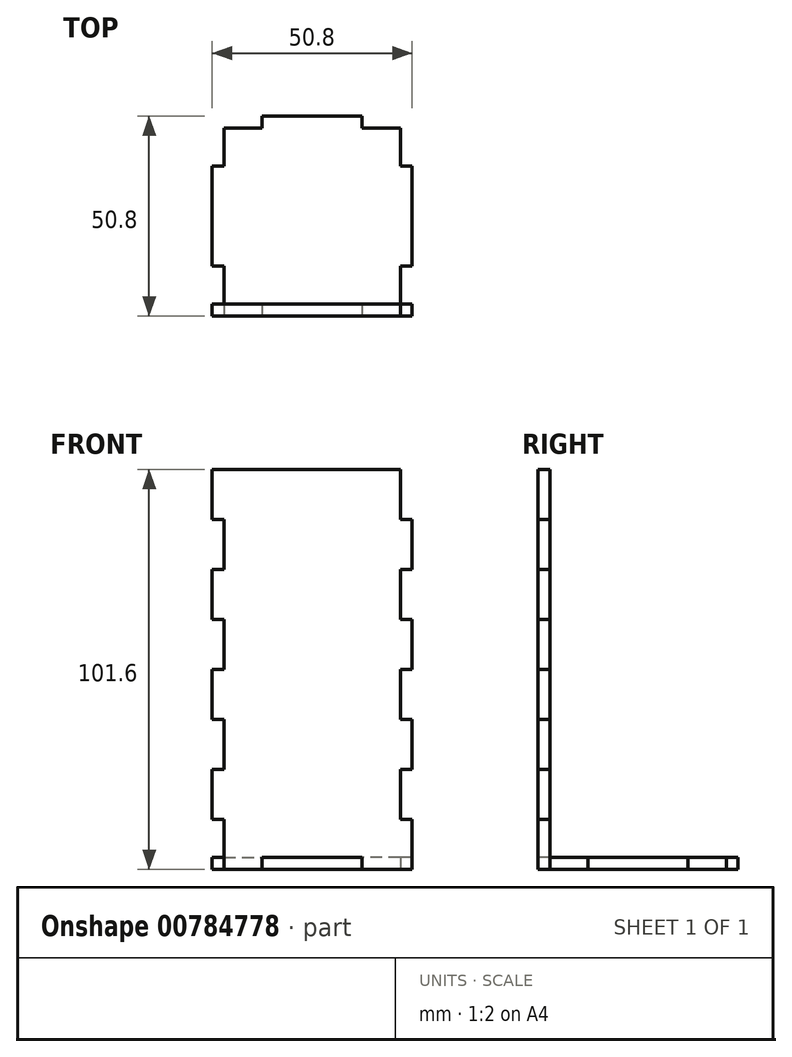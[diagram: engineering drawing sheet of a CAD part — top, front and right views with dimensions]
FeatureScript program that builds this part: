
annotation { "Feature Type Name" : "Feature", "Feature Type Description" : "" }
export const myFeature = defineFeature(function(context is Context, id is Id, definition is map)
    precondition{}
    {
        {
            assignVariable(context, id + "F0", {"variableType" : VariableType.LENGTH, "name" : "thk", "lengthValue" : 3 * mm});
        }
        {
            var Q0;
            Q0=qCreatedBy(makeId("Top.planeOp"),FACE);
            var sketch = newSketch(context, id + "F1", { "sketchPlane" : qUnion([Q0])});
            skLineSegment(sketch, "E0.bottom", {"start": v(25.4, 25.4) * mm, "end": v(-25.4, 25.4) * mm});
            skLineSegment(sketch, "E0.top", {"start": v(25.4, -25.4) * mm, "end": v(-25.4, -25.4) * mm});
            skLineSegment(sketch, "E0.left", {"start": v(25.4, 25.4) * mm, "end": v(25.4, -25.4) * mm});
            skLineSegment(sketch, "E0.right", {"start": v(-25.4, 25.4) * mm, "end": v(-25.4, -25.4) * mm});
            skPoint(sketch, "E0.middle", {"position": v(0, 0) * mm});
            skLineSegment(sketch, "E1", {"start": v(0, 0) * mm, "end": v(-25.4, 0) * mm, "construction": true});
            skLineSegment(sketch, "E2.bottom", {"start": v(-25.4, 25.4) * mm, "end": v(-22.4, 25.4) * mm});
            skLineSegment(sketch, "E2.top", {"start": v(-25.4, 12.7) * mm, "end": v(-22.4, 12.7) * mm});
            skLineSegment(sketch, "E2.left", {"start": v(-25.4, 25.4) * mm, "end": v(-25.4, 12.7) * mm});
            skLineSegment(sketch, "E2.right", {"start": v(-22.4, 25.4) * mm, "end": v(-22.4, 12.7) * mm});
            skLineSegment(sketch, "E3.bottom", {"start": v(-25.4, 25.4) * mm, "end": v(-12.7, 25.4) * mm});
            skLineSegment(sketch, "E3.top", {"start": v(-25.4, 22.4) * mm, "end": v(-12.7, 22.4) * mm});
            skLineSegment(sketch, "E3.left", {"start": v(-25.4, 25.4) * mm, "end": v(-25.4, 22.4) * mm});
            skLineSegment(sketch, "E3.right", {"start": v(-12.7, 25.4) * mm, "end": v(-12.7, 22.4) * mm});
            skLineSegment(sketch, "E4.1.0", {"start": v(-25.4, -25.4) * mm, "end": v(-25.4, -22.4) * mm});
            skLineSegment(sketch, "E4.1.1", {"start": v(-25.4, -22.4) * mm, "end": v(-12.7, -22.4) * mm});
            skLineSegment(sketch, "E4.1.2", {"start": v(-25.4, -25.4) * mm, "end": v(-22.4, -25.4) * mm});
            skLineSegment(sketch, "E4.1.3", {"start": v(-22.4, -25.4) * mm, "end": v(-22.4, -12.7) * mm});
            skLineSegment(sketch, "E4.1.4", {"start": v(-25.4, -25.4) * mm, "end": v(-25.4, -12.7) * mm});
            skLineSegment(sketch, "E4.1.5", {"start": v(-25.4, -12.7) * mm, "end": v(-22.4, -12.7) * mm});
            skLineSegment(sketch, "E4.1.6", {"start": v(-12.7, -25.4) * mm, "end": v(-12.7, -22.4) * mm});
            skLineSegment(sketch, "E4.1.7", {"start": v(-25.4, -25.4) * mm, "end": v(-12.7, -25.4) * mm});
            skLineSegment(sketch, "E4.2.0", {"start": v(25.4, -25.4) * mm, "end": v(22.4, -25.4) * mm});
            skLineSegment(sketch, "E4.2.1", {"start": v(22.4, -25.4) * mm, "end": v(22.4, -12.7) * mm});
            skLineSegment(sketch, "E4.2.2", {"start": v(25.4, -25.4) * mm, "end": v(25.4, -22.4) * mm});
            skLineSegment(sketch, "E4.2.3", {"start": v(25.4, -22.4) * mm, "end": v(12.7, -22.4) * mm});
            skLineSegment(sketch, "E4.2.4", {"start": v(25.4, -25.4) * mm, "end": v(12.7, -25.4) * mm});
            skLineSegment(sketch, "E4.2.5", {"start": v(12.7, -25.4) * mm, "end": v(12.7, -22.4) * mm});
            skLineSegment(sketch, "E4.2.6", {"start": v(25.4, -12.7) * mm, "end": v(22.4, -12.7) * mm});
            skLineSegment(sketch, "E4.2.7", {"start": v(25.4, -25.4) * mm, "end": v(25.4, -12.7) * mm});
            skLineSegment(sketch, "E4.3.0", {"start": v(25.4, 25.4) * mm, "end": v(25.4, 22.4) * mm});
            skLineSegment(sketch, "E4.3.1", {"start": v(25.4, 22.4) * mm, "end": v(12.7, 22.4) * mm});
            skLineSegment(sketch, "E4.3.2", {"start": v(25.4, 25.4) * mm, "end": v(22.4, 25.4) * mm});
            skLineSegment(sketch, "E4.3.3", {"start": v(22.4, 25.4) * mm, "end": v(22.4, 12.7) * mm});
            skLineSegment(sketch, "E4.3.4", {"start": v(25.4, 25.4) * mm, "end": v(25.4, 12.7) * mm});
            skLineSegment(sketch, "E4.3.5", {"start": v(25.4, 12.7) * mm, "end": v(22.4, 12.7) * mm});
            skLineSegment(sketch, "E4.3.6", {"start": v(12.7, 25.4) * mm, "end": v(12.7, 22.4) * mm});
            skLineSegment(sketch, "E4.3.7", {"start": v(25.4, 25.4) * mm, "end": v(12.7, 25.4) * mm});
            skSolve(sketch);
        }
        {
            var Q0;
            {var subQ13=sQuery(id+"F1.wireOp",EDGE,"E2.top");Q0=makeQuery(id+"F1.imprint","IMPRINT",FACE,{"disambiguationData":[TD([[makeQuery(id+"F1.imprint","IMPRINT",EDGE,{"derivedFrom":subQ13}),-1.0]])]});}
            extrude(context, id + "F2", {"entities" : qUnion([Q0]), "depth" : getVariable(context, 'thk'), "offsetDistance" : 25.4 * mm});
        }
        {
            var Q0;
            Q0=makeQuery(id+"F2.opExtrude","SWEPT_FACE",FACE,{"disambiguationData":[OSD([sQuery(id+"F1.wireOp",EDGE,"E0.top")])]});
            var sketch = newSketch(context, id + "F3", { "sketchPlane" : qUnion([Q0])});
            skLineSegment(sketch, "E5.bottom", {"start": v(-25.4, 0) * mm, "end": v(25.4, 0) * mm});
            skLineSegment(sketch, "E5.top", {"start": v(-25.4, 101.6) * mm, "end": v(25.4, 101.6) * mm});
            skLineSegment(sketch, "E5.left", {"start": v(-25.4, 0) * mm, "end": v(-25.4, 101.6) * mm});
            skLineSegment(sketch, "E5.right", {"start": v(25.4, 0) * mm, "end": v(25.4, 101.6) * mm});
            skLineSegment(sketch, "E6", {"start": v(0, 101.6) * mm, "end": v(0, 0) * mm, "construction": true});
            skLineSegment(sketch, "E7", {"start": v(22.4, 101.6) * mm, "end": v(22.4, 0) * mm});
            skLineSegment(sketch, "E8", {"start": v(22.4, 88.9) * mm, "end": v(25.4, 88.9) * mm});
            skLineSegment(sketch, "E9.1.0.0", {"start": v(22.4, 76.2) * mm, "end": v(25.4, 76.2) * mm});
            skLineSegment(sketch, "E9.2.0.0", {"start": v(22.4, 63.5) * mm, "end": v(25.4, 63.5) * mm});
            skLineSegment(sketch, "E9.direction1", {"start": v(22.4, 88.9) * mm, "end": v(22.4, 76.2) * mm, "construction": true});
            skLineSegment(sketch, "E10.0.3.0", {"start": v(22.4, 50.8) * mm, "end": v(25.4, 50.8) * mm});
            skLineSegment(sketch, "E10.0.4.0", {"start": v(22.4, 38.1) * mm, "end": v(25.4, 38.1) * mm});
            skLineSegment(sketch, "E10.0.5.0", {"start": v(22.4, 25.4) * mm, "end": v(25.4, 25.4) * mm});
            skLineSegment(sketch, "E10.0.6.0", {"start": v(22.4, 12.7) * mm, "end": v(25.4, 12.7) * mm});
            skLineSegment(sketch, "E11.MirrorCS", {"start": v(-22.4, 50.8) * mm, "end": v(-25.4, 50.8) * mm});
            skLineSegment(sketch, "E12.MirrorCS", {"start": v(-22.4, 12.7) * mm, "end": v(-25.4, 12.7) * mm});
            skLineSegment(sketch, "E13.MirrorCS", {"start": v(-22.4, 63.5) * mm, "end": v(-25.4, 63.5) * mm});
            skLineSegment(sketch, "E14.MirrorCS", {"start": v(-22.4, 38.1) * mm, "end": v(-25.4, 38.1) * mm});
            skLineSegment(sketch, "E15.MirrorCS", {"start": v(-22.4, 88.9) * mm, "end": v(-25.4, 88.9) * mm});
            skLineSegment(sketch, "E16.MirrorCS", {"start": v(-22.4, 25.4) * mm, "end": v(-25.4, 25.4) * mm});
            skLineSegment(sketch, "E17.MirrorCS", {"start": v(-22.4, 76.2) * mm, "end": v(-25.4, 76.2) * mm});
            skLineSegment(sketch, "E18.MirrorCS", {"start": v(-22.4, 88.9) * mm, "end": v(-22.4, 76.2) * mm, "construction": true});
            skLineSegment(sketch, "E19.MirrorCS", {"start": v(-22.4, 101.6) * mm, "end": v(-22.4, 0) * mm});
            skSolve(sketch);
        }
        {
            var Q0;
            {var subQ15=sQuery(id+"F1.wireOp",EDGE,"E0.top");Q0=makeQuery(id+"F3.imprint","IMPRINT",FACE,{"disambiguationData":[TD([[makeQuery(id+"F3.imprint","IMPRINT",EDGE,{"derivedFrom":makeQuery(id+"F2.opExtrude","CAP_EDGE",EDGE,{"disambiguationData":[OSD([subQ15])],"isStart":false})}),-1.0]])]});}
            var Q1;
            {var subQ5=sQuery(id+"F3.wireOp",EDGE,"E10.0.6.0");Q1=makeQuery(id+"F3.imprint","IMPRINT",FACE,{"disambiguationData":[TD([[makeQuery(id+"F3.imprint","IMPRINT",EDGE,{"derivedFrom":subQ5}),-1.0]])]});}
            var Q2;
            {var subQ0=sQuery(id+"F3.wireOp",EDGE,"E10.0.4.0");Q2=makeQuery(id+"F3.imprint","IMPRINT",FACE,{"disambiguationData":[TD([[makeQuery(id+"F3.imprint","IMPRINT",EDGE,{"derivedFrom":subQ0}),-1.0]])]});}
            var Q3;
            {var subQ0=sQuery(id+"F3.wireOp",EDGE,"E9.2.0.0");Q3=makeQuery(id+"F3.imprint","IMPRINT",FACE,{"disambiguationData":[TD([[makeQuery(id+"F3.imprint","IMPRINT",EDGE,{"derivedFrom":subQ0}),-1.0]])]});}
            var Q4;
            {var subQ0=sQuery(id+"F3.wireOp",EDGE,"E8");Q4=makeQuery(id+"F3.imprint","IMPRINT",FACE,{"disambiguationData":[TD([[makeQuery(id+"F3.imprint","IMPRINT",EDGE,{"derivedFrom":subQ0}),-1.0]])]});}
            var Q5;
            {var subQ0=sQuery(id+"F3.wireOp",EDGE,"E12.MirrorCS");Q5=makeQuery(id+"F3.imprint","IMPRINT",FACE,{"disambiguationData":[TD([[makeQuery(id+"F3.imprint","IMPRINT",EDGE,{"derivedFrom":subQ0}),-1.0]])]});}
            var Q6;
            {var subQ0=sQuery(id+"F3.wireOp",EDGE,"E11.MirrorCS");Q6=makeQuery(id+"F3.imprint","IMPRINT",FACE,{"disambiguationData":[TD([[makeQuery(id+"F3.imprint","IMPRINT",EDGE,{"derivedFrom":subQ0}),1.0]])]});}
            var Q7;
            {var subQ0=sQuery(id+"F3.wireOp",EDGE,"E13.MirrorCS");Q7=makeQuery(id+"F3.imprint","IMPRINT",FACE,{"disambiguationData":[TD([[makeQuery(id+"F3.imprint","IMPRINT",EDGE,{"derivedFrom":subQ0}),-1.0]])]});}
            var Q8;
            {var subQ5=sQuery(id+"F3.wireOp",EDGE,"E15.MirrorCS");Q8=makeQuery(id+"F3.imprint","IMPRINT",FACE,{"disambiguationData":[TD([[makeQuery(id+"F3.imprint","IMPRINT",EDGE,{"derivedFrom":subQ5}),-1.0]])]});}
            extrude(context, id + "F4", {"entities" : qUnion([Q0, Q1, Q2, Q3, Q4, Q5, Q6, Q7, Q8]), "oppositeDirection" : true, "depth" : getVariable(context, 'thk'), "offsetDistance" : 25.4 * mm});
        }
    });
